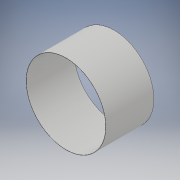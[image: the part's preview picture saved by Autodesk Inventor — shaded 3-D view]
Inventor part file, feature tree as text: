
AUTODESK INVENTOR PART (.ipt)
format: ipt  version: 2019 (Build 230136000, 136)  size: 103,424 bytes
history: native  units: mm
features: extrude x2, sketch x2
ambient origin geometry x8: Origin, YZ Plane, XZ Plane, XY Plane, X Axis, Y Axis, Z Axis, Center Point
bodies: Solid1 (feature_tree)
feature tree (4):
  extrude  "Extrusion1"  Depth=12.02mm TaperAngle=0.0deg
  extrude  "Extrusion2"  Depth=12.02mm TaperAngle=0.0deg
  sketch  "Sketch1"  dims[d0=19.97mm d1=12.02mm d2=0.0mm]
  sketch  "Sketch2"  dims[d3=19.87mm d4=12.02mm d5=0.0mm]
